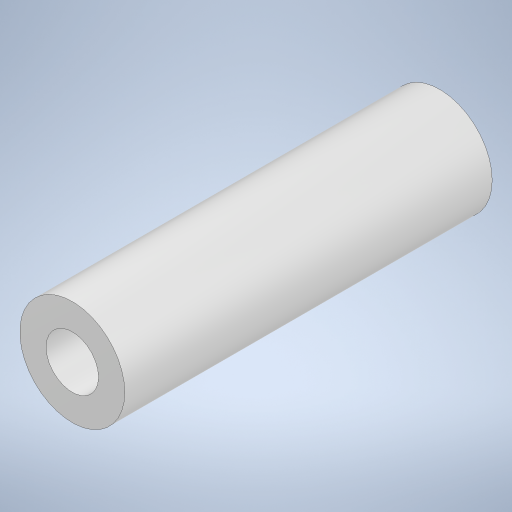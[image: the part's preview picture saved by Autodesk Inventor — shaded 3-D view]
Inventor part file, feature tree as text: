
AUTODESK INVENTOR PART (.ipt)
format: ipt  version: 2023 (Build 270158030, 158C)  size: 224,256 bytes
history: native  units: mm
features: other x1, extrude x1, sketch x1
ambient origin geometry x8: Origin, YZ Plane, XZ Plane, XY Plane, X Axis, Y Axis, Z Axis, Center Point
bodies: Body1 (feature_tree)
feature tree (3):
  other  "ソリッド1"
  extrude  "押し出し1"  Depth=6.0mm
  sketch  "スケッチ1"
